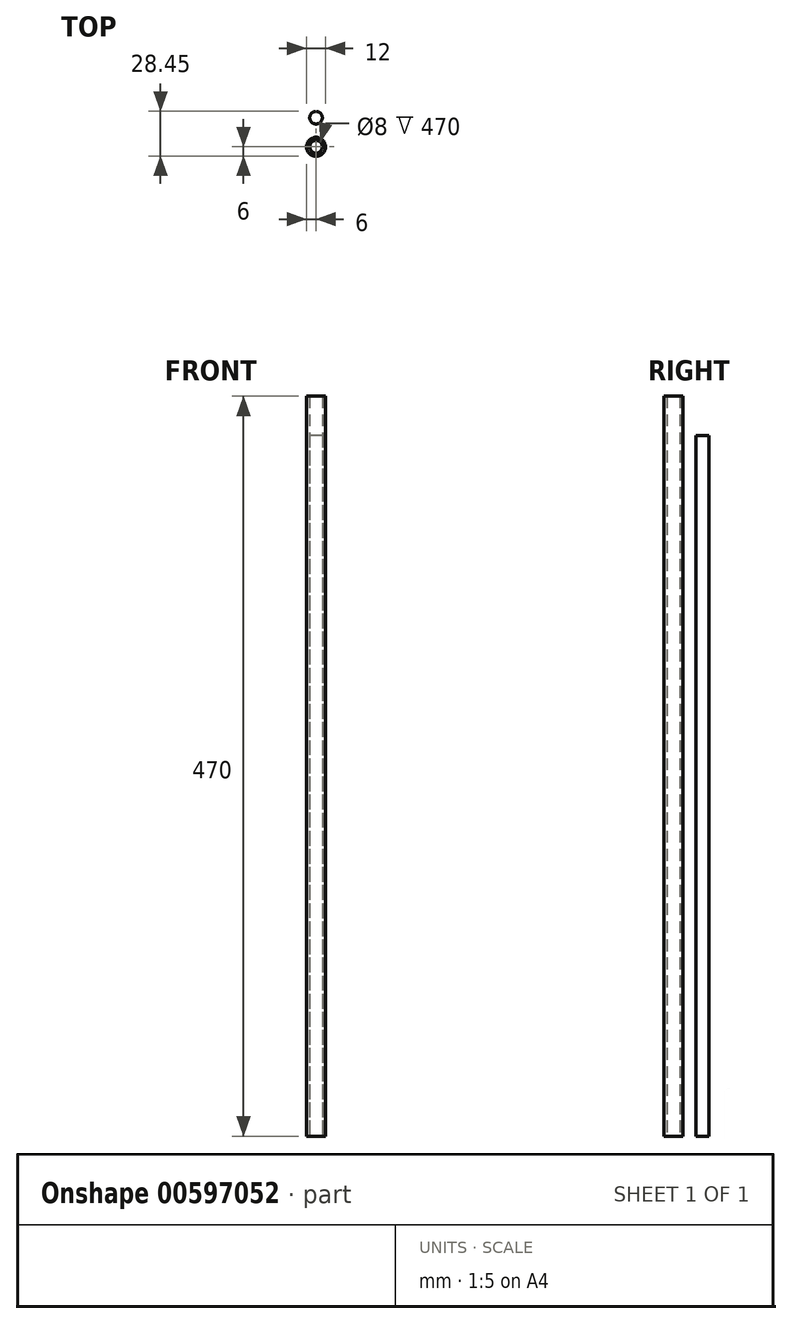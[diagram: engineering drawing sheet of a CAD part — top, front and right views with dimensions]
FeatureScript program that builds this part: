
annotation { "Feature Type Name" : "Feature", "Feature Type Description" : "" }
export const myFeature = defineFeature(function(context is Context, id is Id, definition is map)
    precondition{}
    {
        {
            var Q0;
            Q0=qCreatedBy(makeId("Top.planeOp"),FACE);
            var sketch = newSketch(context, id + "F0", { "sketchPlane" : qUnion([Q0])});
            skCircle(sketch, "E0", {"center": v(0, 0) * mm, "radius": 6 * mm});
            skCircle(sketch, "E1", {"center": v(0, 0) * mm, "radius": 4 * mm});
            skSolve(sketch);
        }
        {
            var Q0;
            Q0=qSketchRegion(id+"F0",true);
            extrude(context, id + "F1", {"entities" : qUnion([Q0]), "depth" : 470 * mm});
        }
        {
            var Q0;
            Q0=qCreatedBy(makeId("Top.planeOp"),FACE);
            var sketch = newSketch(context, id + "F2", { "sketchPlane" : qUnion([Q0])});
            skCircle(sketch, "E2", {"center": v(0, 18.45) * mm, "radius": 4 * mm});
            skSolve(sketch);
        }
        {
            var Q0;
            Q0=makeQuery(id+"F2.imprint","IMPRINT",FACE,{"disambiguationData":[TD([[makeQuery(id+"F2.imprint","IMPRINT",EDGE,{"derivedFrom":sQuery(id+"F2.wireOp",EDGE,"E2")}),1.0]])]});
            extrude(context, id + "F3", {"entities" : qUnion([Q0]), "depth" : 445 * mm});
        }
    });
